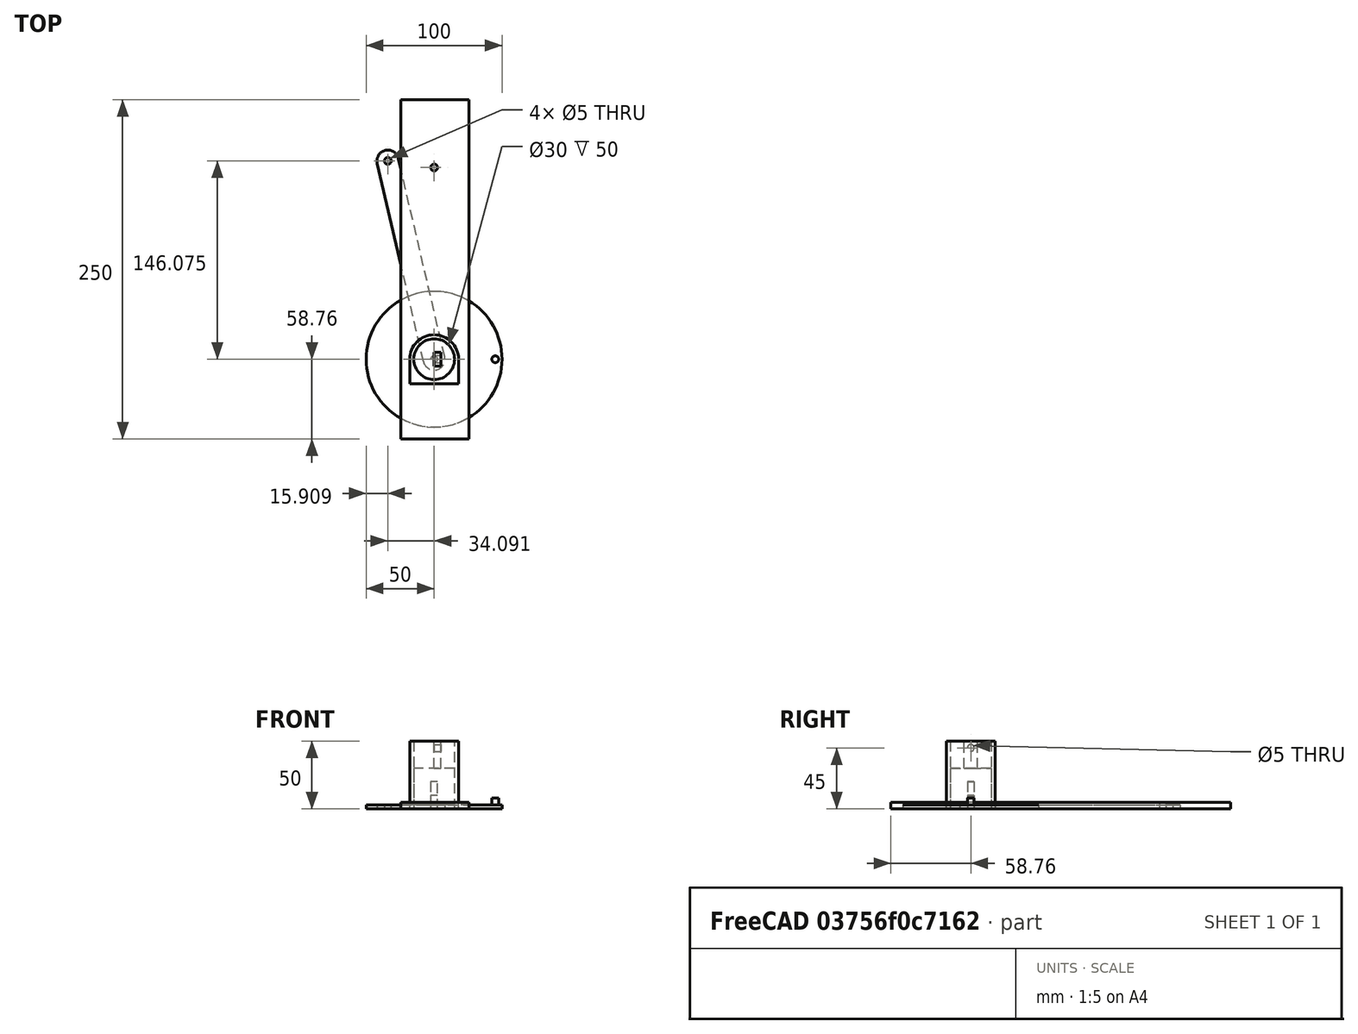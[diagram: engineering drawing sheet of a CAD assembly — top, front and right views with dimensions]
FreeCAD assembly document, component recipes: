
FREECAD ASSEMBLY — COMPONENT RECIPES ("Ass_12")

This assembly document has 10 components, labeled P0..P9 below (a component is one placed body or linked part). 9 of them carry a construction recipe — the FreeCAD feature program that regenerates the part from scratch, quoted from this document or its linked companion documents; the rest are supplied as boundary geometry only. No exploded tour is included for this assembly.
COMPONENT P0 — geometry summary ("Assembly"; no construction recipe available for this part):
  bounding box: 250.7 x 96.6 x 38.6 mm
  tessellated surface: 260 triangles
  volume: 168837209302325616699114642879846377299568459162905229879046083780689890521029220503243561113781010432 mm^3 (18069380130286296620183499984974918604263647975420765648616604038289973984013162305875016171913216% of its bounding box)
COMPONENT P1 — recipe-attached ("Body_blin_2", modeled in this document).
Construction recipe (the document's own serialized feature program — sketch geometry with constraints, then the solid features built on it; lengths are millimeters unless a unit is written):

FEATURE [Sketcher::SketchObject] Sketch
  FullyConstrained = true
  MapMode = 5
  Support = -> [XY_Plane001]
  sketch-geometry (2):
    g0: Circle CenterX=0 CenterY=0 CenterZ=0 NormalX=0 NormalY=0 NormalZ=1 AngleXU=0 Radius=50
    g1: Circle CenterX=0 CenterY=0 CenterZ=0 NormalX=0 NormalY=0 NormalZ=1 AngleXU=0 Radius=2.5
  constraints (4):
    c: Coincident(g0,g-1)
    c: Diameter(g0) = 100
    c: Coincident(g1,g0)
    c: Diameter(g1) = 5
FEATURE [PartDesign::Pad] Pad
  Direction = (1,1,1)
  Length = 3
  Length2 = 100
  Profile = -> Sketch
  Type = 0
FEATURE [Sketcher::SketchObject] Sketch001
  FullyConstrained = true
  MapMode = 5
  Placement = pos=(0,0,3) rot=(0,0,1;0rad)
  Support = -> [Pad]
  sketch-geometry (1):
    g0: Circle CenterX=45 CenterY=0 CenterZ=0 NormalX=0 NormalY=0 NormalZ=1 AngleXU=0 Radius=2.5
  constraints (3):
    c: PointOnObject(g0,g-1)
    c: Distance(g-1,g0) = 45
    c: Diameter(g0) = 5
FEATURE [PartDesign::Pad] Pad001
  BaseFeature = -> Pad
  Direction = (1,1,1)
  Length = 5
  Length2 = 100
  Profile = -> Sketch001
  Type = 0
FEATURE [PartDesign::CoordinateSystem] LCS_Blin_Center
  AttacherType = Attacher::AttachEngine3D
  MapMode = 11
  Placement = pos=(0,0,3) rot=(0,0,1;1.5708rad)
  Support = -> [Pad001]
FEATURE [PartDesign::Body] Body  label="Body_blin_2"
  Group = -> [Sketch,Pad,Sketch001,Pad001,LCS_Blin_Center]
  Origin = -> Origin001
  Tip = -> Pad001
COMPONENT P2 — recipe-attached ("Body_piston", modeled in this document).
Construction recipe (the document's own serialized feature program — sketch geometry with constraints, then the solid features built on it; lengths are millimeters unless a unit is written):

FEATURE [Sketcher::SketchObject] Sketch003
  FullyConstrained = true
  MapMode = 5
  Support = -> [XY_Plane003]
  sketch-geometry (1):
    g0: Circle CenterX=0 CenterY=0 CenterZ=0 NormalX=0 NormalY=0 NormalZ=1 AngleXU=0 Radius=15
  constraints (2):
    c: Coincident(g0,g-1)
    c: Diameter(g0) = 30
FEATURE [PartDesign::Pad] Pad003
  Direction = (1,1,1)
  Length = 30
  Length2 = 100
  Profile = -> Sketch003
  Type = 0
FEATURE [Sketcher::SketchObject] Sketch004
  FullyConstrained = true
  MapMode = 5
  Placement = pos=(0,0,30) rot=(0,0,1;0rad)
  Support = -> [Pad003]
  sketch-geometry (4):
    g0: LineSegment StartX=0 StartY=5 StartZ=0 EndX=5 EndY=5 EndZ=0
    g1: LineSegment StartX=5 StartY=5 StartZ=0 EndX=5 EndY=-5 EndZ=0
    g2: LineSegment StartX=5 StartY=-5 StartZ=0 EndX=0 EndY=-5 EndZ=0
    g3: LineSegment StartX=0 StartY=-5 StartZ=0 EndX=0 EndY=5 EndZ=0
  constraints (11):
    c: Coincident(g0,g1)
    c: Coincident(g1,g2)
    c: Coincident(g2,g3)
    c: Coincident(g3,g0)
    c: Horizontal(g0)
    c: Horizontal(g2)
    c: Vertical(g1)
    c: Vertical(g3)
    c: Symmetric(g2,g0,g-1)
    c: DistanceX(g0,g0) = 5
    c: DistanceY(g1,g1) = 10
FEATURE [PartDesign::Pad] Pad004
  BaseFeature = -> Pad003
  Direction = (1,1,1)
  Length = 20
  Length2 = 100
  Profile = -> Sketch004
  Type = 0
FEATURE [Sketcher::SketchObject] Sketch005
  FullyConstrained = true
  MapMode = 5
  Placement = pos=(5,0,0) rot=(0.57735,0.57735,0.57735;2.0944rad)
  Support = -> [Pad004]
  sketch-geometry (1):
    g0: Circle CenterX=0 CenterY=45 CenterZ=0 NormalX=0 NormalY=0 NormalZ=1 AngleXU=0 Radius=2.5
  constraints (3):
    c: PointOnObject(g0,g-2)
    c: Diameter(g0) = 5
    c: DistanceY(g-1,g0) = 45
FEATURE [PartDesign::Pocket] Pocket
  BaseFeature = -> Pad004
  Length = 5
  Length2 = 100
  Profile = -> Sketch005
  Type = 1
FEATURE [PartDesign::CoordinateSystem] LCS_Piston_1
  AttacherType = Attacher::AttachEngine3D
  MapMode = 11
  Placement = pos=(0,0,45) rot=(0.707107,0,0.707107;3.14159rad)
  Support = -> [Pocket]
FEATURE [PartDesign::Body] Body002  label="Body_piston"
  Group = -> [Sketch003,Pad003,Sketch004,Pad004,Sketch005,Pocket,LCS_Piston_1]
  Origin = -> Origin003
  Tip = -> Pocket
COMPONENT P3 — recipe-attached ("Body_Shtift_5x10_", modeled in this document).
Construction recipe (the document's own serialized feature program — sketch geometry with constraints, then the solid features built on it; lengths are millimeters unless a unit is written):

FEATURE [Sketcher::SketchObject] Sketch006
  FullyConstrained = true
  MapMode = 5
  Support = -> [XY_Plane004]
  sketch-geometry (1):
    g0: Circle CenterX=0 CenterY=0 CenterZ=0 NormalX=0 NormalY=0 NormalZ=1 AngleXU=0 Radius=2.5
  constraints (2):
    c: Coincident(g0,g-1)
    c: Diameter(g0) = 5
FEATURE [PartDesign::Pad] Pad005
  Direction = (1,1,1)
  Length = 10
  Length2 = 100
  Profile = -> Sketch006
  Type = 0
FEATURE [PartDesign::CoordinateSystem] LCS_Shtift_center
  AttacherType = Attacher::AttachEngine3D
  MapMode = 11
  Placement = pos=(0,0,10) rot=(0,0,1;1.5708rad)
  Support = -> [Pad005]
FEATURE [PartDesign::Body] Body003  label="Body_Shtift_5x10_"
  Group = -> [Sketch006,Pad005,LCS_Shtift_center]
  Origin = -> Origin004
  Tip = -> Pad005
COMPONENT P4 — recipe-attached ("Body_Shtift_5x10", modeled in this document).
Construction recipe (the document's own serialized feature program — sketch geometry with constraints, then the solid features built on it; lengths are millimeters unless a unit is written):

FEATURE [Sketcher::SketchObject] Sketch008
  FullyConstrained = true
  MapMode = 5
  Support = -> [XY_Plane006]
  sketch-geometry (1):
    g0: Circle CenterX=0 CenterY=0 CenterZ=0 NormalX=0 NormalY=0 NormalZ=1 AngleXU=0 Radius=2.5
  constraints (2):
    c: Coincident(g0,g-1)
    c: Diameter(g0) = 5
FEATURE [PartDesign::Pad] Pad007
  Direction = (1,1,1)
  Length = 10
  Length2 = 100
  Profile = -> Sketch008
  Type = 0
FEATURE [PartDesign::CoordinateSystem] LCS_Shtift_5x10_Center
  AttacherType = Attacher::AttachEngine3D
  MapMode = 11
  Placement = pos=(0,0,10) rot=(0,0,1;1.5708rad)
  Support = -> [Pad007]
FEATURE [PartDesign::Body] Body005  label="Body_Shtift_5x10"
  Group = -> [Sketch008,Pad007,LCS_Shtift_5x10_Center]
  Origin = -> Origin006
  Tip = -> Pad007
COMPONENT P5 — recipe-attached ("Body_cilinder_Sq", modeled in this document).
Construction recipe (the document's own serialized feature program — sketch geometry with constraints, then the solid features built on it; lengths are millimeters unless a unit is written):

FEATURE [Sketcher::SketchObject] Sketch009
  FullyConstrained = false
  MapMode = 5
  Support = -> [XY_Plane007]
  sketch-geometry (5):
    g0: ArcOfCircle CenterX=0 CenterY=0 CenterZ=0 NormalX=0 NormalY=0 NormalZ=1 AngleXU=0 Radius=18 StartAngle=0 EndAngle=3.14159
    g1: Circle CenterX=0 CenterY=0 CenterZ=0 NormalX=0 NormalY=0 NormalZ=1 AngleXU=0 Radius=15
    g2: LineSegment StartX=18 StartY=0 StartZ=0 EndX=18 EndY=-18 EndZ=0
    g3: LineSegment StartX=18 StartY=-18 StartZ=0 EndX=-18 EndY=-18 EndZ=0
    g4: LineSegment StartX=-18 StartY=-18 StartZ=0 EndX=-18 EndY=0 EndZ=0
  constraints (9):
    c: Coincident(g0,g-1)
    c: Coincident(g1,g0)
    c: Diameter(g1) = 30
    c: Diameter(g0) = 36
    c: Coincident(g2,g3)
    c: Coincident(g3,g4)
    c: Horizontal(g3)
    c: Vertical(g2)
    c: Vertical(g4)
FEATURE [PartDesign::Pad] Pad008
  Direction = (1,1,1)
  Length = 50
  Length2 = 100
  Profile = -> Sketch009
  Type = 0
FEATURE [PartDesign::CoordinateSystem] LCS_Cilinder_center
  AttacherType = Attacher::AttachEngine3D
  MapMode = 11
  Placement = pos=(0,0,50) rot=(0,0,1;1.5708rad)
  Support = -> [Pad008]
FEATURE [PartDesign::Body] Body006  label="Body_cilinder_Sq"
  Group = -> [Sketch009,Pad008,LCS_Cilinder_center]
  Origin = -> Origin007
  Tip = -> Pad008
COMPONENT P6 — recipe-attached ("Body_osnovanie", modeled in this document).
Construction recipe (the document's own serialized feature program — sketch geometry with constraints, then the solid features built on it; lengths are millimeters unless a unit is written):

FEATURE [Sketcher::SketchObject] Sketch010
  FullyConstrained = false
  MapMode = 5
  Support = -> [XY_Plane008]
  sketch-geometry (5):
    g0: LineSegment StartX=25.5407 StartY=-58.7601 StartZ=0 EndX=-24.4593 EndY=-58.7601 EndZ=0
    g1: LineSegment StartX=-24.4593 StartY=-58.7601 StartZ=0 EndX=-24.4593 EndY=191.24 EndZ=0
    g2: LineSegment StartX=-24.4593 StartY=191.24 StartZ=0 EndX=25.5407 EndY=191.24 EndZ=0
    g3: LineSegment StartX=25.5407 StartY=191.24 StartZ=0 EndX=25.5407 EndY=-58.7601 EndZ=0
    g4: Circle CenterX=0 CenterY=141.24 CenterZ=0 NormalX=0 NormalY=0 NormalZ=1 AngleXU=0 Radius=2.5
  constraints (13):
    c: Coincident(g0,g1)
    c: Coincident(g1,g2)
    c: Coincident(g2,g3)
    c: Coincident(g3,g0)
    c: Horizontal(g0)
    c: Horizontal(g2)
    c: Vertical(g1)
    c: Vertical(g3)
    c: DistanceY(g3,g3) = 250
    c: DistanceX(g2,g2) = 50
    c: PointOnObject(g4,g-2)
    c: Diameter(g4) = 5
    c: DistanceY(g0,g4) = 200
FEATURE [PartDesign::Pad] Pad009
  Direction = (1,1,1)
  Length = 5
  Length2 = 100
  Profile = -> Sketch010
  Type = 0
FEATURE [PartDesign::CoordinateSystem] LCS_osnov_W
  AttacherType = Attacher::AttachEngine3D
  MapMode = 11
  Placement = pos=(0,141.24,5) rot=(0,0,1;1.5708rad)
  Support = -> [Pad009]
FEATURE [PartDesign::Body] Body007  label="Body_osnovanie"
  Group = -> [Sketch010,Pad009,LCS_osnov_W]
  Origin = -> Origin008
  Tip = -> Pad009
COMPONENT P7 — recipe-attached ("Body_Shtift_5x20", modeled in this document).
Construction recipe (the document's own serialized feature program — sketch geometry with constraints, then the solid features built on it; lengths are millimeters unless a unit is written):

FEATURE [Sketcher::SketchObject] Sketch011
  FullyConstrained = true
  MapMode = 5
  Support = -> [XY_Plane009]
  sketch-geometry (1):
    g0: Circle CenterX=0 CenterY=0 CenterZ=0 NormalX=0 NormalY=0 NormalZ=1 AngleXU=0 Radius=2.5
  constraints (2):
    c: Coincident(g0,g-1)
    c: Diameter(g0) = 5
FEATURE [PartDesign::Pad] Pad010
  Direction = (1,1,1)
  Length = 20
  Length2 = 100
  Profile = -> Sketch011
  Type = 0
FEATURE [PartDesign::CoordinateSystem] LCS_Shtift_W_Center
  AttacherType = Attacher::AttachEngine3D
  MapMode = 11
  Placement = pos=(0,0,20) rot=(0,0,1;1.5708rad)
  Support = -> [Pad010]
FEATURE [PartDesign::CoordinateSystem] LCS_Shitt_W_center
  AttacherType = Attacher::AttachEngine3D
  MapMode = 11
  Placement = pos=(0,0,0) rot=(0,0,1;1.5708rad)
  Support = -> [Pad010]
FEATURE [PartDesign::Body] Body008  label="Body_Shtift_5x20"
  Group = -> [Sketch011,Pad010,LCS_Shtift_W_Center,LCS_Shitt_W_center]
  Origin = -> Origin009
  Tip = -> Pad010
COMPONENT P8 — recipe-attached ("Body_blin_003", modeled in this document).
Construction recipe (the document's own serialized feature program — sketch geometry with constraints, then the solid features built on it; lengths are millimeters unless a unit is written):

FEATURE [Sketcher::SketchObject] Sketch012
  FullyConstrained = true
  MapMode = 5
  Support = -> [XY_Plane010]
  sketch-geometry (2):
    g0: Circle CenterX=0 CenterY=0 CenterZ=0 NormalX=0 NormalY=0 NormalZ=1 AngleXU=0 Radius=50
    g1: Circle CenterX=0 CenterY=0 CenterZ=0 NormalX=0 NormalY=0 NormalZ=1 AngleXU=0 Radius=2.5
  constraints (4):
    c: Coincident(g0,g-1)
    c: Diameter(g0) = 100
    c: Coincident(g1,g0)
    c: Diameter(g1) = 5
FEATURE [PartDesign::Pad] Pad011
  Direction = (1,1,1)
  Length = 3
  Length2 = 100
  Profile = -> Sketch012
  Type = 0
FEATURE [Sketcher::SketchObject] Sketch013
  FullyConstrained = true
  MapMode = 5
  Placement = pos=(0,0,3) rot=(0,0,1;0rad)
  Support = -> [Pad011]
  sketch-geometry (1):
    g0: Circle CenterX=45 CenterY=0 CenterZ=0 NormalX=0 NormalY=0 NormalZ=1 AngleXU=0 Radius=2.5
  constraints (3):
    c: PointOnObject(g0,g-1)
    c: Distance(g-1,g0) = 45
    c: Diameter(g0) = 5
FEATURE [PartDesign::Pad] Pad012
  BaseFeature = -> Pad011
  Direction = (1,1,1)
  Length = 5
  Length2 = 100
  Profile = -> Sketch013
  Type = 0
FEATURE [PartDesign::CoordinateSystem] LCS_Blin_Center001
  AttacherType = Attacher::AttachEngine3D
  MapMode = 11
  Placement = pos=(0,0,3) rot=(0,0,1;1.5708rad)
  Support = -> [Pad012]
FEATURE [PartDesign::CoordinateSystem] LCS_Blin_Rad
  AttacherType = Attacher::AttachEngine3D
  MapMode = 11
  Placement = pos=(45,0,3) rot=(0,0,1;1.5708rad)
  Support = -> [Pad012]
FEATURE [PartDesign::Body] Body009  label="Body_blin_003"
  Group = -> [Sketch012,Pad011,Sketch013,Pad012,LCS_Blin_Center001,LCS_Blin_Rad]
  Origin = -> Origin010
  Tip = -> Pad012
COMPONENT P9 — recipe-attached ("Body_Shatun", modeled in this document).
Construction recipe (the document's own serialized feature program — sketch geometry with constraints, then the solid features built on it; lengths are millimeters unless a unit is written):

FEATURE [Sketcher::SketchObject] Sketch014
  FullyConstrained = false
  MapMode = 5
  Support = -> [XY_Plane011]
  sketch-geometry (6):
    g0: ArcOfCircle CenterX=0 CenterY=0 CenterZ=0 NormalX=0 NormalY=0 NormalZ=1 AngleXU=0 Radius=8 StartAngle=3.37087 EndAngle=6.51246
    g1: ArcOfCircle CenterX=-34.091 CenterY=146.075 CenterZ=0 NormalX=0 NormalY=0 NormalZ=1 AngleXU=0 Radius=8 StartAngle=0.229277 EndAngle=3.37087
    g2: LineSegment StartX=7.79065 StartY=1.81819 StartZ=0 EndX=-26.3003 EndY=147.893 EndZ=0
    g3: LineSegment StartX=-7.79065 StartY=-1.81819 StartZ=0 EndX=-41.8816 EndY=144.256 EndZ=0
    g4: Circle CenterX=0 CenterY=0 CenterZ=0 NormalX=0 NormalY=0 NormalZ=1 AngleXU=0 Radius=2.5
    g5: Circle CenterX=-34.091 CenterY=146.075 CenterZ=0 NormalX=0 NormalY=0 NormalZ=1 AngleXU=0 Radius=2.5
  constraints (12):
    c: Tangent(g0,g3) = 1.5708
    c: Tangent(g0,g2) = -1.5708
    c: Tangent(g2,g1) = -1.5708
    c: Tangent(g3,g1) = 1.5708
    c: Equal(g0,g1)
    c: Coincident(g4,g0)
    c: Coincident(g5,g1)
    c: Equal(g4,g5)
    c: Diameter(g5) = 5
    c: Radius(g0) = 8
    c: Coincident(g0,g-1)
    c: Distance(g1,g0) = 150
FEATURE [PartDesign::Pad] Pad013
  Direction = (1,1,1)
  Length = 3
  Length2 = 100
  Profile = -> Sketch014
  Type = 0
FEATURE [PartDesign::CoordinateSystem] LCS_SH_W001  label="LCS_SH_W"
  AttacherType = Attacher::AttachEngine3D
  MapMode = 11
  Placement = pos=(-34.091,146.075,3) rot=(0,0,1;1.5708rad)
  Support = -> [Pad013]
FEATURE [PartDesign::CoordinateSystem] LCS_SH_P
  AttacherType = Attacher::AttachEngine3D
  MapMode = 11
  Placement = pos=(0,0,3) rot=(0,0,1;1.5708rad)
  Support = -> [Pad013]
FEATURE [PartDesign::Body] Body010  label="Body_Shatun"
  Group = -> [Sketch014,Pad013,LCS_SH_W001,LCS_SH_P]
  Origin = -> Origin011
  Tip = -> Pad013
PROVENANCE & LICENSES
A FreeCAD (.FCStd) document from a public repository crawl; recipes are the document's own serialized feature recipes (and, for linked parts, companion documents' recipes).
License: as declared in the source repository (recorded in the dataset sidecar).
